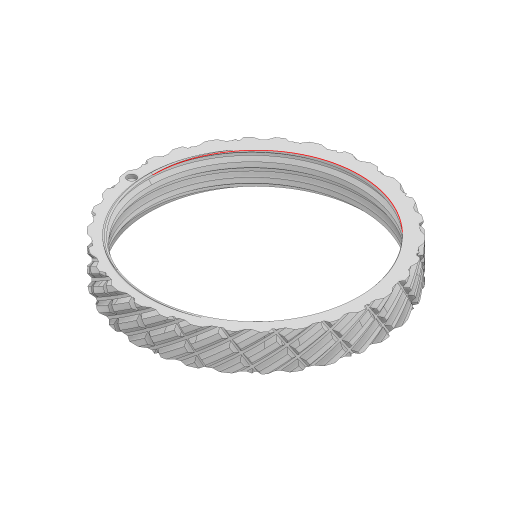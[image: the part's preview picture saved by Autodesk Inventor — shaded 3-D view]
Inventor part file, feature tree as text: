
AUTODESK INVENTOR PART (.ipt)
format: ipt  version: 2023 (Build 270158000, 158)  size: 1,638,400 bytes
history: native  units: mm
features: helix x6, sketch x3, pattern_circular x2, revolve x1, hole x1, direct_edit x1, other x1
ambient origin geometry x8: Origin, YZ Plane, XZ Plane, XY Plane, X Axis, Y Axis, Z Axis, Center Point
bodies: Solid1 (feature_tree)
feature tree (15):
  sketch  "Sketch1"  dims[d0=13.0mm d1=1.2mm d2=16.755161mm d3=12.875mm d4=2.2mm d5=5.0mm d6=90.0deg d7=2.0mm d8=5.0mm d9=10.0mm d10=-1.047198mm]
  revolve  "Revolution1"  [1 undecoded]
  helix  "Coil1"  [1 undecoded]
  helix  "Coil2"  [1 undecoded]
  sketch  "Sketch3"  dims[d11=90.0deg d12=90.0deg d13=0.0mm d14=0.0mm]
  helix  "Coil3"  [1 undecoded]
  helix  "Coil4"  [1 undecoded]
  pattern_circular  "Circular Pattern1"  [2 undecoded]
  helix  "Coil5"  [1 undecoded]
  helix  "Coil6"  [1 undecoded]
  pattern_circular  "Circular Pattern2"  [2 undecoded]
  hole  "Hole1"  [1 undecoded]
  direct_edit  "Direct Edit1"
  sketch  "Sketch4"  dims[d15=2.0mm d16=5.0mm d17=10.0mm d18=1.047198mm d19=90.0deg d20=90.0deg d21=0.0mm d22=0.0mm d37=0.5mm d39=0.5mm d41=1.5mm d42=6.981317mm d43=6.981317mm d44=0.707706mm d45=0.707706mm d46=70.0mm d47=10.0mm d48=10.0mm d49=0.0mm d50=90.0deg d51=90.0deg d52=0.0mm d53=0.0mm d54=70.0mm d55=10.0mm d56=10.0mm d57=0.0mm d58=90.0deg d59=90.0deg d60=0.0mm d61=0.0mm d62=300.0mm d63=360.0deg d65=150.0mm d66=10.0mm d67=10.0mm d68=0.0mm d69=90.0deg d70=90.0deg d71=0.0mm d72=0.0mm d73=150.0mm d74=10.0mm d75=10.0mm d76=0.0mm d77=90.0deg d78=90.0deg d79=0.0mm d80=0.0mm d81=200.0mm d82=360.0deg d84=1.2mm d85=6.0mm d86=4.0mm d87=2.0mm d88=90.0deg d89=0.5mm d90=0.0mm d91=-0.254mm d92=14.660766mm]
  other  "Size1"
note: 12 required parameter values undecoded (feature->parameter linkage not recoverable at this tier; creation-order binding heuristic only, values carry confidence <= 0.55)